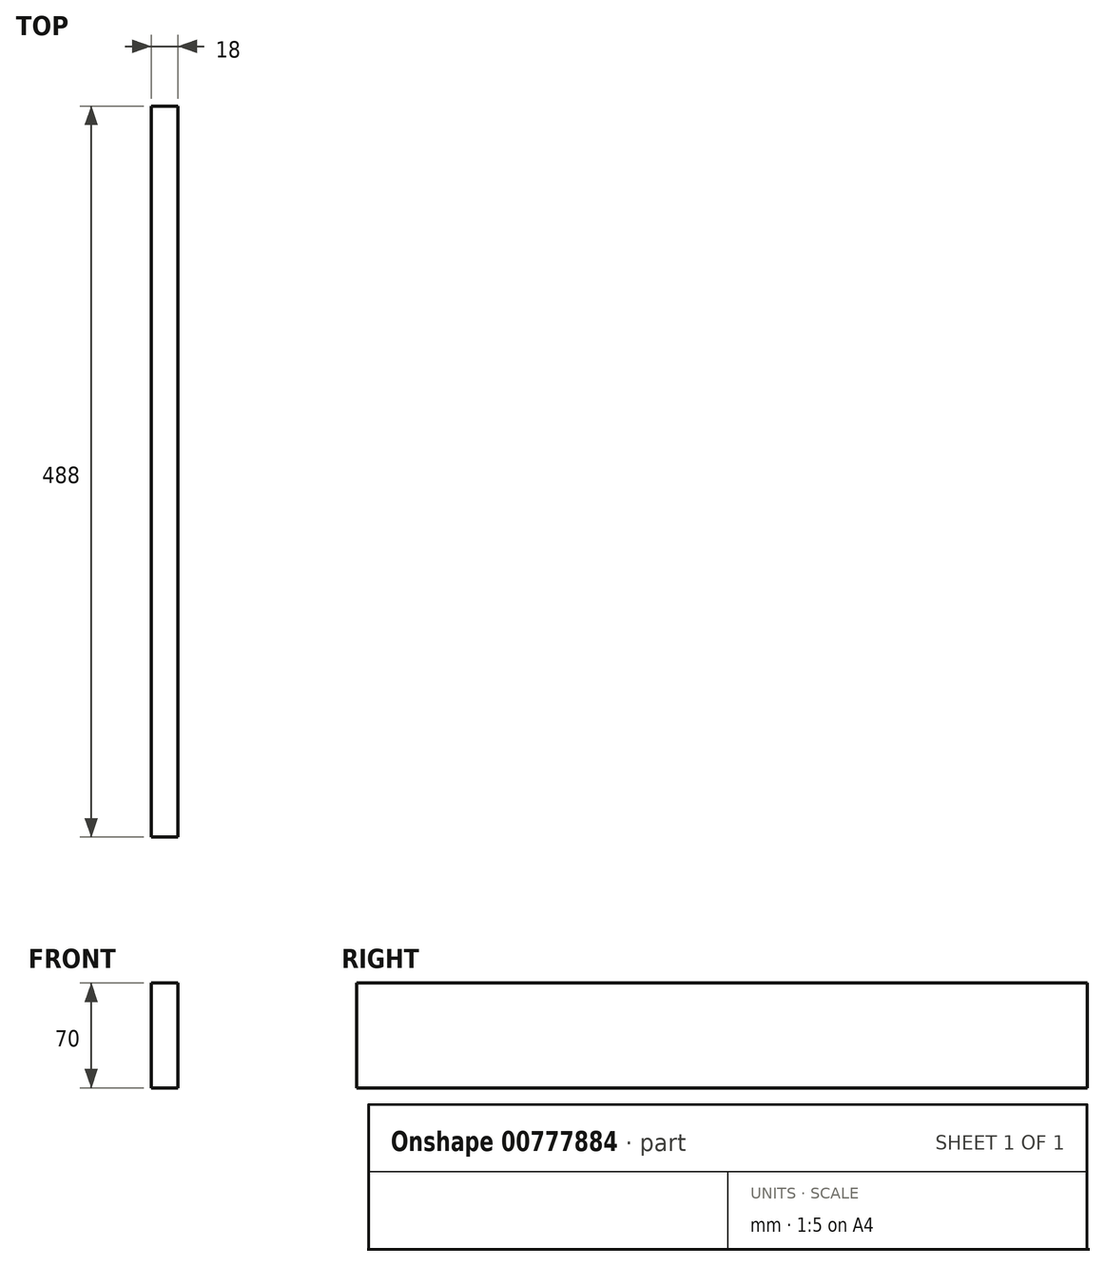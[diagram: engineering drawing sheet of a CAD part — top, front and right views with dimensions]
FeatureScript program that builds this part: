
annotation { "Feature Type Name" : "Feature", "Feature Type Description" : "" }
export const myFeature = defineFeature(function(context is Context, id is Id, definition is map)
    precondition{}
    {
        {
            var Q0;
            Q0=qCreatedBy(makeId("Right.planeOp"),FACE);
            var sketch = newSketch(context, id + "F0", { "sketchPlane" : qUnion([Q0])});
            skLineSegment(sketch, "E0.bottom", {"start": v(-244, 35) * mm, "end": v(244, 35) * mm});
            skLineSegment(sketch, "E0.top", {"start": v(-244, -35) * mm, "end": v(244, -35) * mm});
            skLineSegment(sketch, "E0.left", {"start": v(-244, 35) * mm, "end": v(-244, -35) * mm});
            skLineSegment(sketch, "E0.right", {"start": v(244, 35) * mm, "end": v(244, -35) * mm});
            skSolve(sketch);
        }
        {
            var Q0;
            Q0 = qSketchRegion(id + "F0", true);
            extrude(context, id + "F1", {"entities" : qUnion([Q0]), "endBound" : BoundingType.SYMMETRIC, "depth" : 18 * mm, "offsetDistance" : 25 * mm});
        }
    });
